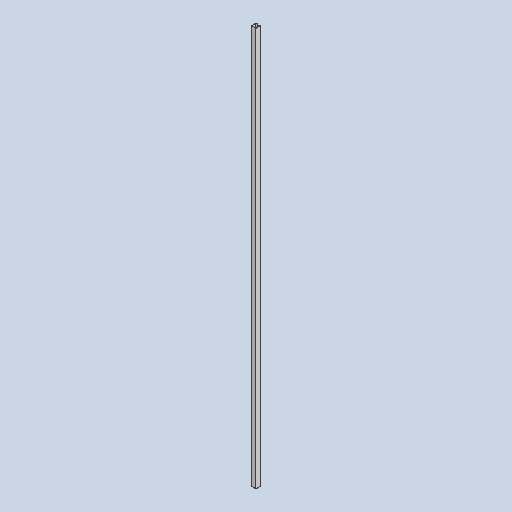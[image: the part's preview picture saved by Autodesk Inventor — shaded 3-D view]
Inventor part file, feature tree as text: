
AUTODESK INVENTOR PART (.ipt)
format: ipt  version: 2023 (Build 270158000, 158)  size: 138,240 bytes
history: native  units: mm
features: extrude x2, sketch x2, projected_geometry x2
ambient origin geometry x8: Origin, YZ Plane, XZ Plane, XY Plane, X Axis, Y Axis, Z Axis, Center Point
bodies: Solid1 (feature_tree)
feature tree (6):
  extrude  "Extrusion1"  Depth=30.0mm
  extrude  "Extrusion2"  Depth=10.0mm
  sketch  "Sketch1"  dims[d0=30.0mm d1=30.0mm]
  sketch  "Sketch2"  dims[d2=2.0mm d3=10.0mm d4=30.0mm d5=15.0mm d6=2560.0mm d7=0.0mm d8=510.0mm d9=15.0mm d10=510.0mm d11=15.0mm d12=2.0mm d13=0.0mm]
  projected_geometry  "Projected Loop1"
  projected_geometry  "Projected Loop2"
